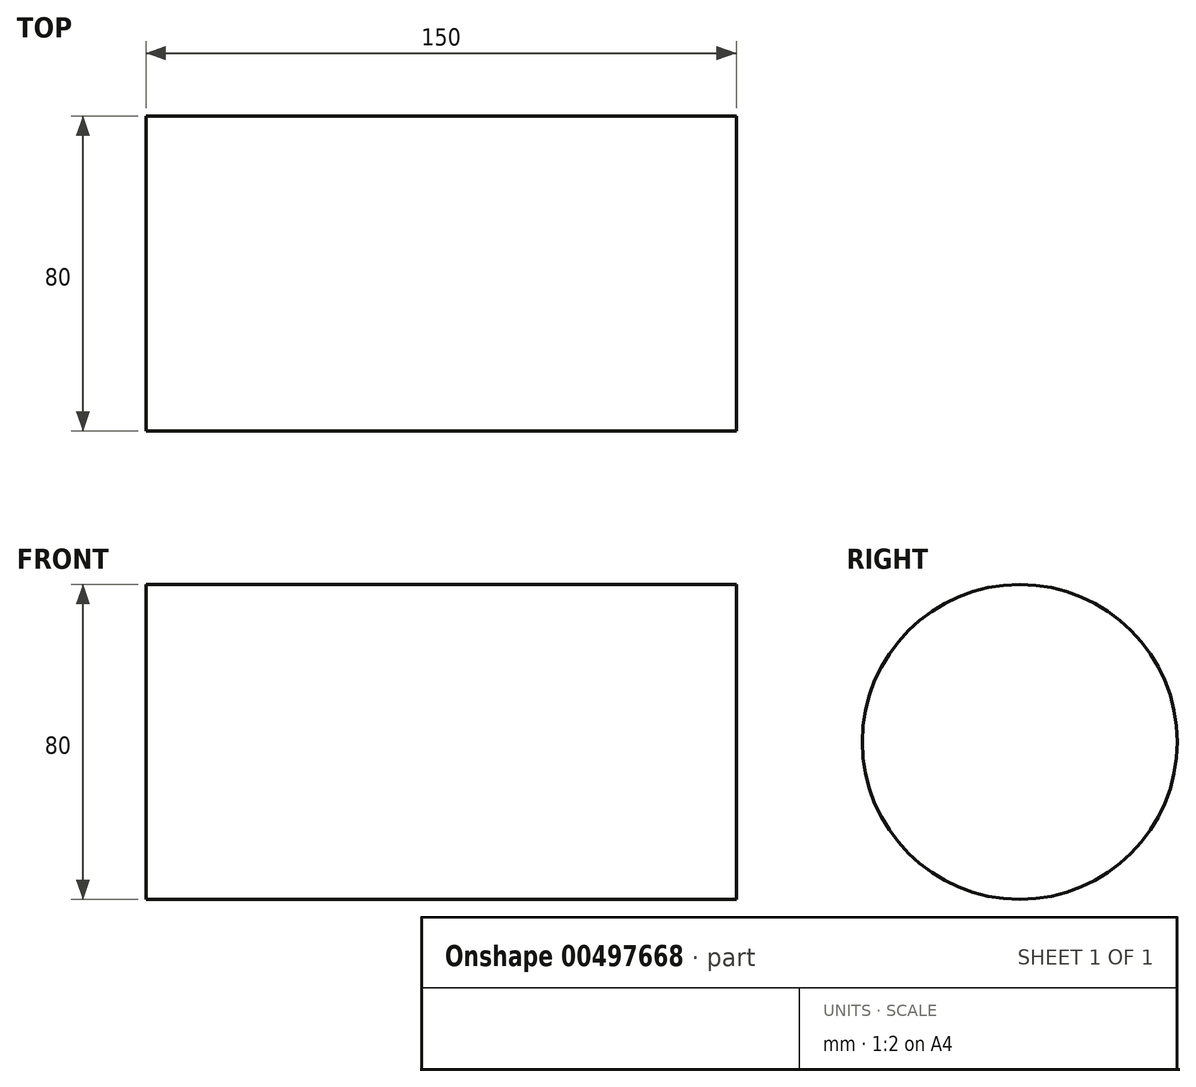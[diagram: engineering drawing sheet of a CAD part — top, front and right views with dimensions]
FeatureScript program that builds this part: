
annotation { "Feature Type Name" : "Feature", "Feature Type Description" : "" }
export const myFeature = defineFeature(function(context is Context, id is Id, definition is map)
    precondition{}
    {
        {
            var Q0;
            Q0=qCreatedBy(makeId("Front.planeOp"),FACE);
            var sketch = newSketch(context, id + "F0", { "sketchPlane" : qUnion([Q0])});
            skLineSegment(sketch, "E0", {"start": v(0, 0) * mm, "end": v(0, 40) * mm});
            skLineSegment(sketch, "E1", {"start": v(0, 40) * mm, "end": v(-150, 40) * mm});
            skLineSegment(sketch, "E2", {"start": v(-150, 40) * mm, "end": v(-150, 0) * mm});
            skLineSegment(sketch, "E3", {"start": v(-150, 0) * mm, "end": v(0, 0) * mm});
            skPoint(sketch, "E4.orphan", {"position": v(-173.36, 0) * mm});
            skSolve(sketch);
        }
        {
            var Q0;
            Q0=makeQuery(id+"F0.imprint","IMPRINT",FACE,{"disambiguationData":[TD([[makeQuery(id+"F0.imprint","IMPRINT",EDGE,{"derivedFrom":sQuery(id+"F0.wireOp",EDGE,"E0")}),1.0]])]});
            var Q1;
            Q1=sQuery(id+"F0.wireOp",EDGE,"E3");
            revolve(context, id + "F1", {"entities" : qUnion([Q0]), "axis" : qUnion([Q1]), "revolveType" : RevolveType.FULL});
        }
    });
